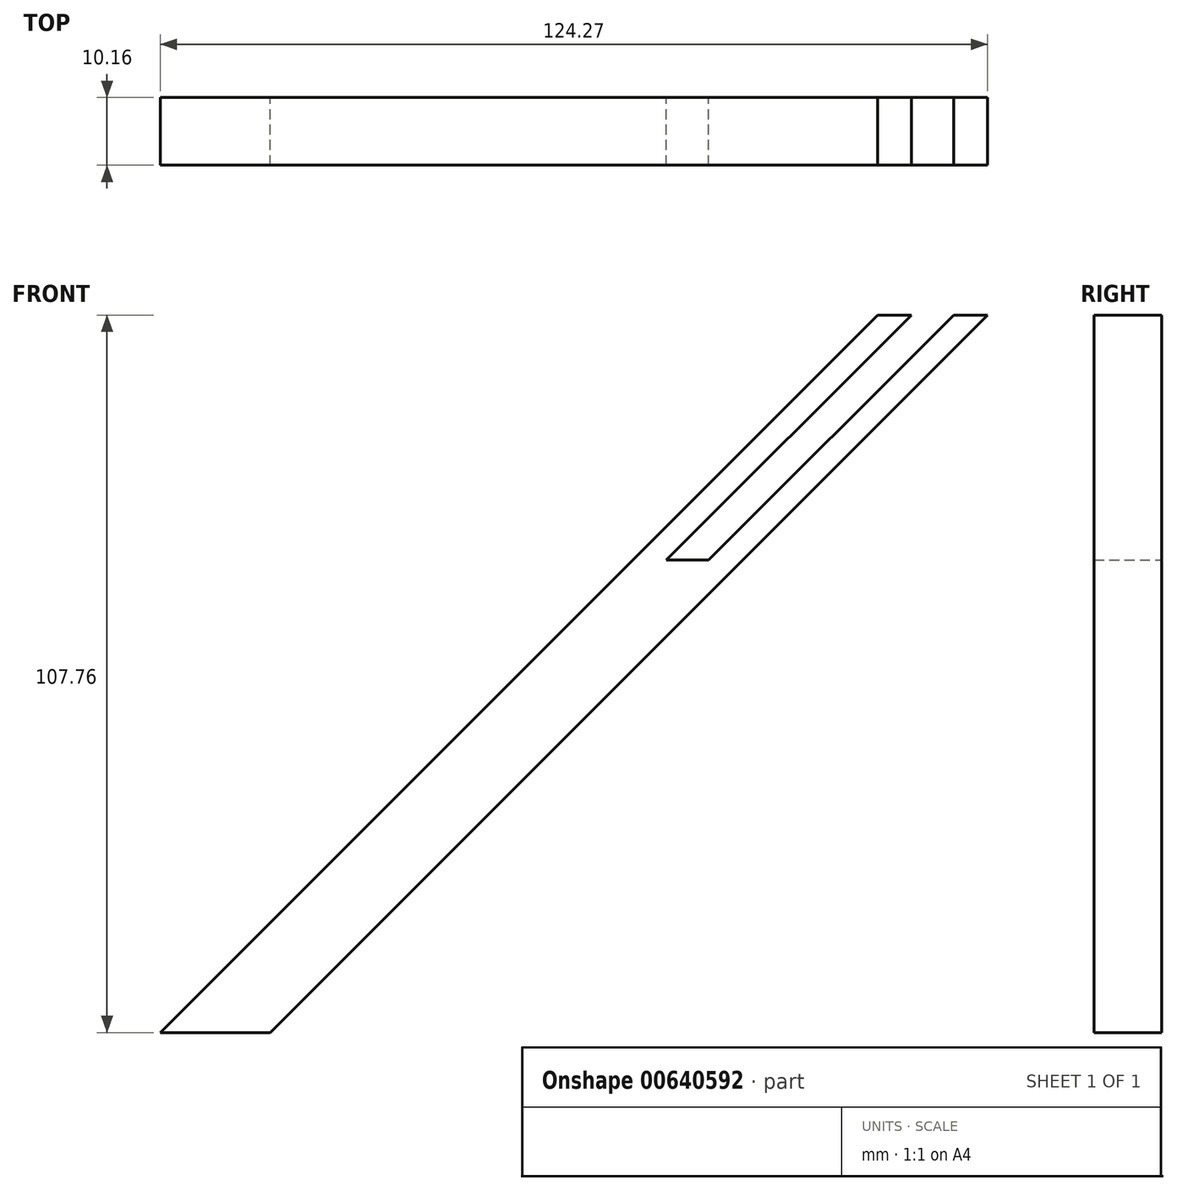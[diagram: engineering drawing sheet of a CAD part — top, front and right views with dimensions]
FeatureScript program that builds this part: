
annotation { "Feature Type Name" : "Feature", "Feature Type Description" : "" }
export const myFeature = defineFeature(function(context is Context, id is Id, definition is map)
    precondition{}
    {
        {
            var Q0;
            Q0=qCreatedBy(makeId("Front.planeOp"),FACE);
            var sketch = newSketch(context, id + "F0", { "sketchPlane" : qUnion([Q0])});
            skLineSegment(sketch, "E0", {"start": v(0, 0) * mm, "end": v(16.51, 0) * mm});
            skLineSegment(sketch, "E1", {"start": v(0, 0) * mm, "end": v(107.76, 107.76) * mm});
            skLineSegment(sketch, "E2", {"start": v(107.76, 107.76) * mm, "end": v(112.84, 107.76) * mm});
            skLineSegment(sketch, "E3", {"start": v(112.84, 107.76) * mm, "end": v(76.02, 70.94) * mm});
            skLineSegment(sketch, "E4", {"start": v(76.02, 70.94) * mm, "end": v(82.37, 70.94) * mm});
            skLineSegment(sketch, "E5", {"start": v(82.37, 70.94) * mm, "end": v(119.2, 107.76) * mm});
            skLineSegment(sketch, "E6", {"start": v(119.2, 107.76) * mm, "end": v(124.27, 107.76) * mm});
            skLineSegment(sketch, "E7", {"start": v(124.27, 107.76) * mm, "end": v(16.51, 0) * mm});
            skSolve(sketch);
        }
        {
            var Q0;
            Q0=makeQuery(id+"F0.imprint","IMPRINT",FACE,{"disambiguationData":[TD([[makeQuery(id+"F0.imprint","IMPRINT",EDGE,{"derivedFrom":sQuery(id+"F0.wireOp",EDGE,"E0")}),1.0]])]});
            extrude(context, id + "F1", {"entities" : qUnion([Q0]), "depth" : 10.16 * mm, "offsetDistance" : 25.4 * mm});
        }
    });
